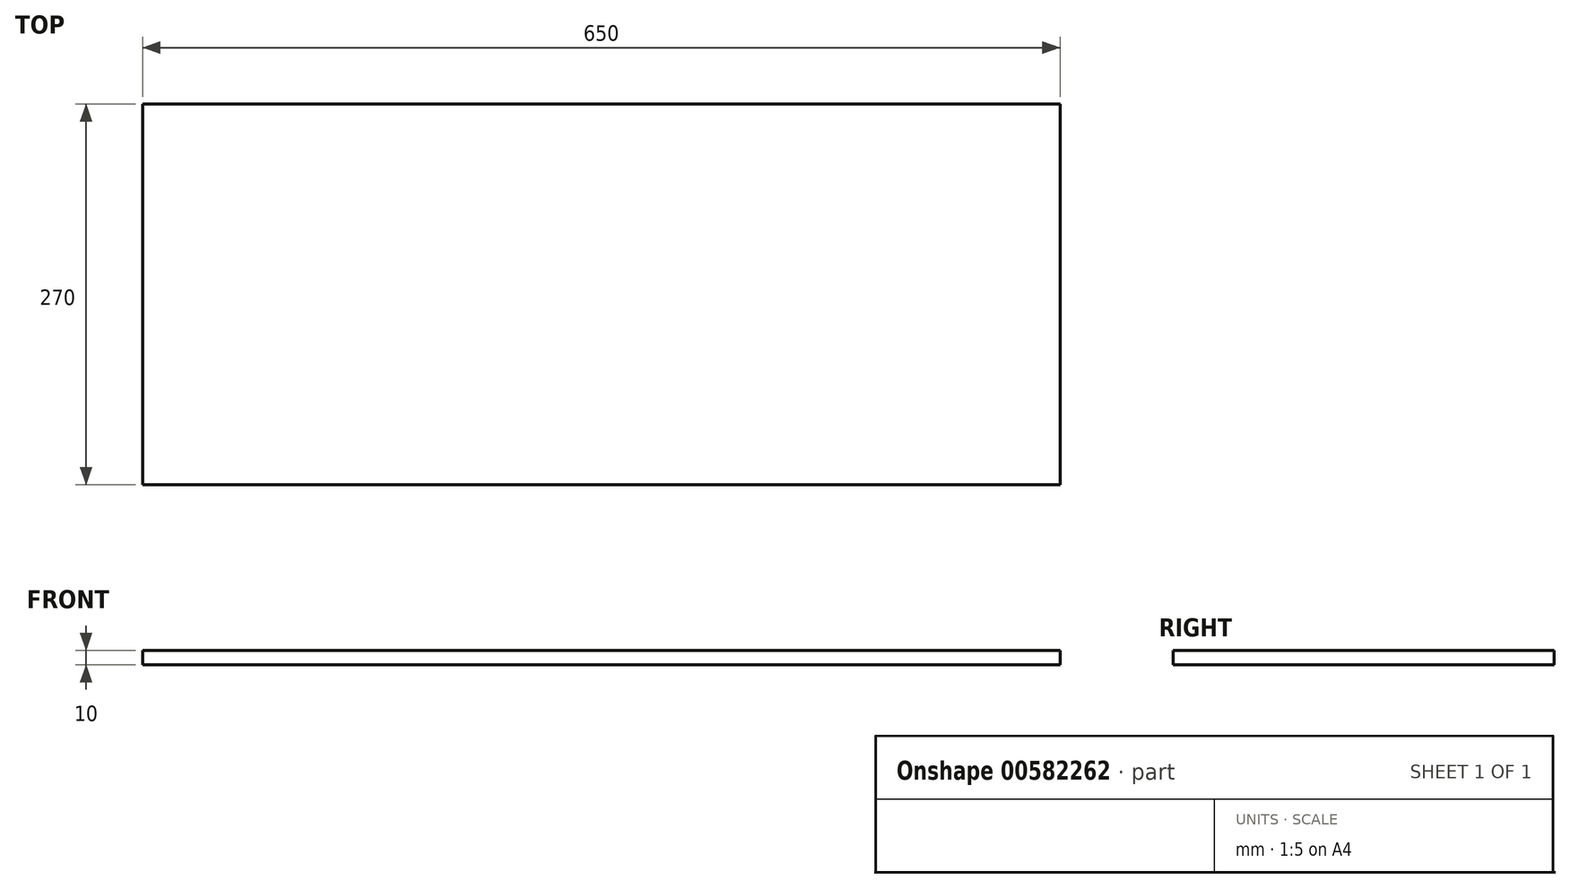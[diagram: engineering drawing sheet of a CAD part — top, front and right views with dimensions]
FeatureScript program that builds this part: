
annotation { "Feature Type Name" : "Feature", "Feature Type Description" : "" }
export const myFeature = defineFeature(function(context is Context, id is Id, definition is map)
    precondition{}
    {
        {
            var Q0;
            Q0=qCreatedBy(makeId("Top.planeOp"),FACE);
            var sketch = newSketch(context, id + "F0", { "sketchPlane" : qUnion([Q0])});
            skLineSegment(sketch, "E0.bottom", {"start": v(325, -135) * mm, "end": v(-325, -135) * mm});
            skLineSegment(sketch, "E0.top", {"start": v(325, 135) * mm, "end": v(-325, 135) * mm});
            skLineSegment(sketch, "E0.left", {"start": v(325, -135) * mm, "end": v(325, 135) * mm});
            skLineSegment(sketch, "E0.right", {"start": v(-325, -135) * mm, "end": v(-325, 135) * mm});
            skPoint(sketch, "E0.middle", {"position": v(0, 0) * mm});
            skSolve(sketch);
        }
        {
            var Q0;
            Q0 = qSketchRegion(id + "F0", true);
            extrude(context, id + "F1", {"entities" : qUnion([Q0]), "depth" : 10 * mm, "offsetDistance" : 25 * mm});
        }
    });
